# Revit family: Caroma Liano Above Counter Basin
name_source: partatom
category: Plumbing Fixtures
revit_build: Autodesk Revit LT 2014 (Build: 20130308_1515(x64)
units: mm (PartAtom-declared; Revit-internal decimal feet)

## types (1)
- Liano Above Counter - 3 Tap Holes
    1 Taphole = No
    3 Tapholes = Yes
    Assembly Code = D2010310
    CW Connection = No
    Cost = 445 $
    Default Elevation = 0 mm  [stored 0 ft]
    Depth_ANZRS = 170 mm  [stored 0.557743 ft]
    Description = Caroma Liano Above Counter Basin
    HW Connection = No
    Keynote = WB
    Length_ANZRS = 420 mm  [stored 1.37795 ft]
    Manufacturer = GWA Bathrooms & Kitchens
    Material_ANZRS = Porcelain-White-Caroma
    Model = 664435W
    ModifiedIssue_ANZRS = 20140919.01 $
    Spout Penetration = 10 mm  [stored 0.0328084 ft]
    Tap Penetrations = 10 mm  [stored 0.0328084 ft]
    Type Comments = Capacity: 4.8L to overflow, Overflow available only, Bracket included, White plug and chrome flush fitting waste included
    URL = http://www.caroma.com.au
    Vent Connection = No
    WFU = 2
    Waste = Metal-Chrome-Caroma
    Waste Connection = Yes
    WasteOutlet_ANZRS = 0
    Width_ANZRS = 470 mm  [stored 1.54199 ft]

note: [stored X ft] marks values corroborated as IEEE doubles in the binary element streams (Revit-internal decimal feet)

## geometry (parser evidence)
native form markers: Blend x8, Sweep x1
no freeform markers — native parametric forms only
